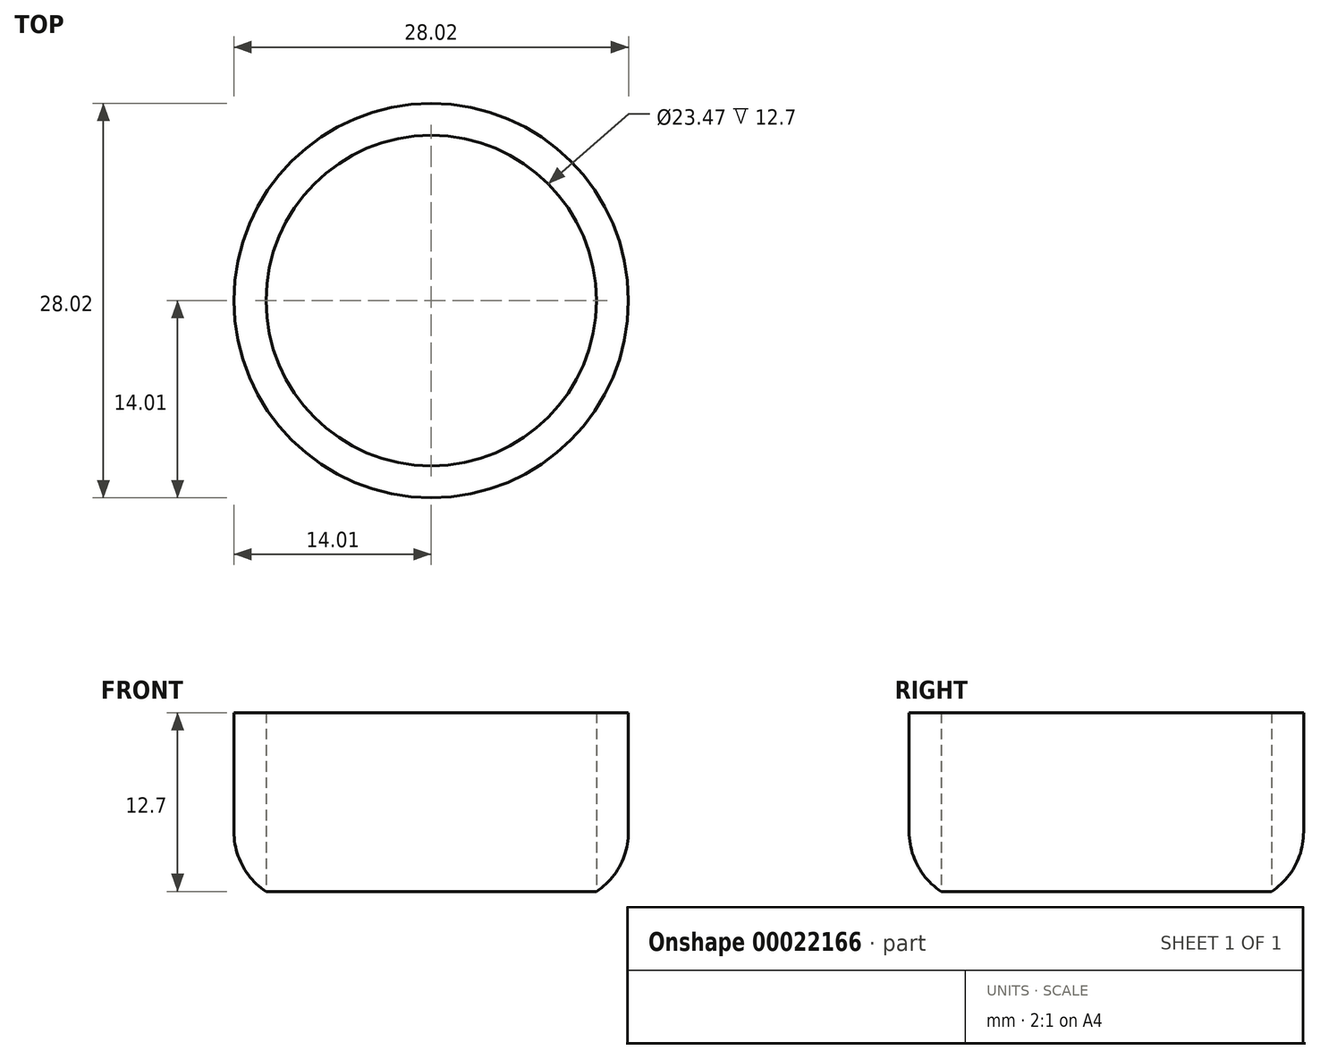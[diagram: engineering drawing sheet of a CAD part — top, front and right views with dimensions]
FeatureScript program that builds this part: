
annotation { "Feature Type Name" : "Feature", "Feature Type Description" : "" }
export const myFeature = defineFeature(function(context is Context, id is Id, definition is map)
    precondition{}
    {
        {
            var Q0;
            Q0=qCreatedBy(makeId("Top.planeOp"),FACE);
            var sketch = newSketch(context, id + "F0", { "sketchPlane" : qUnion([Q0])});
            skCircle(sketch, "E0", {"center": v(0, 0) * mm, "radius": 14 * mm});
            skCircle(sketch, "E1", {"center": v(0, 0) * mm, "radius": 11.73 * mm});
            skSolve(sketch);
        }
        {
            var Q0;
            Q0=makeQuery(id+"F0.imprint","IMPRINT",FACE,{"disambiguationData":[TD([[makeQuery(id+"F0.imprint","IMPRINT",EDGE,{"derivedFrom":sQuery(id+"F0.wireOp",EDGE,"E0")}),1.0]])]});
            extrude(context, id + "F1", {"entities" : qUnion([Q0]), "depth" : 12.7 * mm});
        }
        {
            var Q0;
            Q0=makeQuery(id+"F1.opExtrude","CAP_EDGE",EDGE,{"disambiguationData":[OSD([sQuery(id+"F0.wireOp",EDGE,"E0")])],"isStart":true});
            fillet(context, id + "F2", {"entities" : qUnion([Q0]), "radius" : 5.08 * mm, "tangentPropagation" : true, "allowEdgeOverflow" : false});
        }
    });
